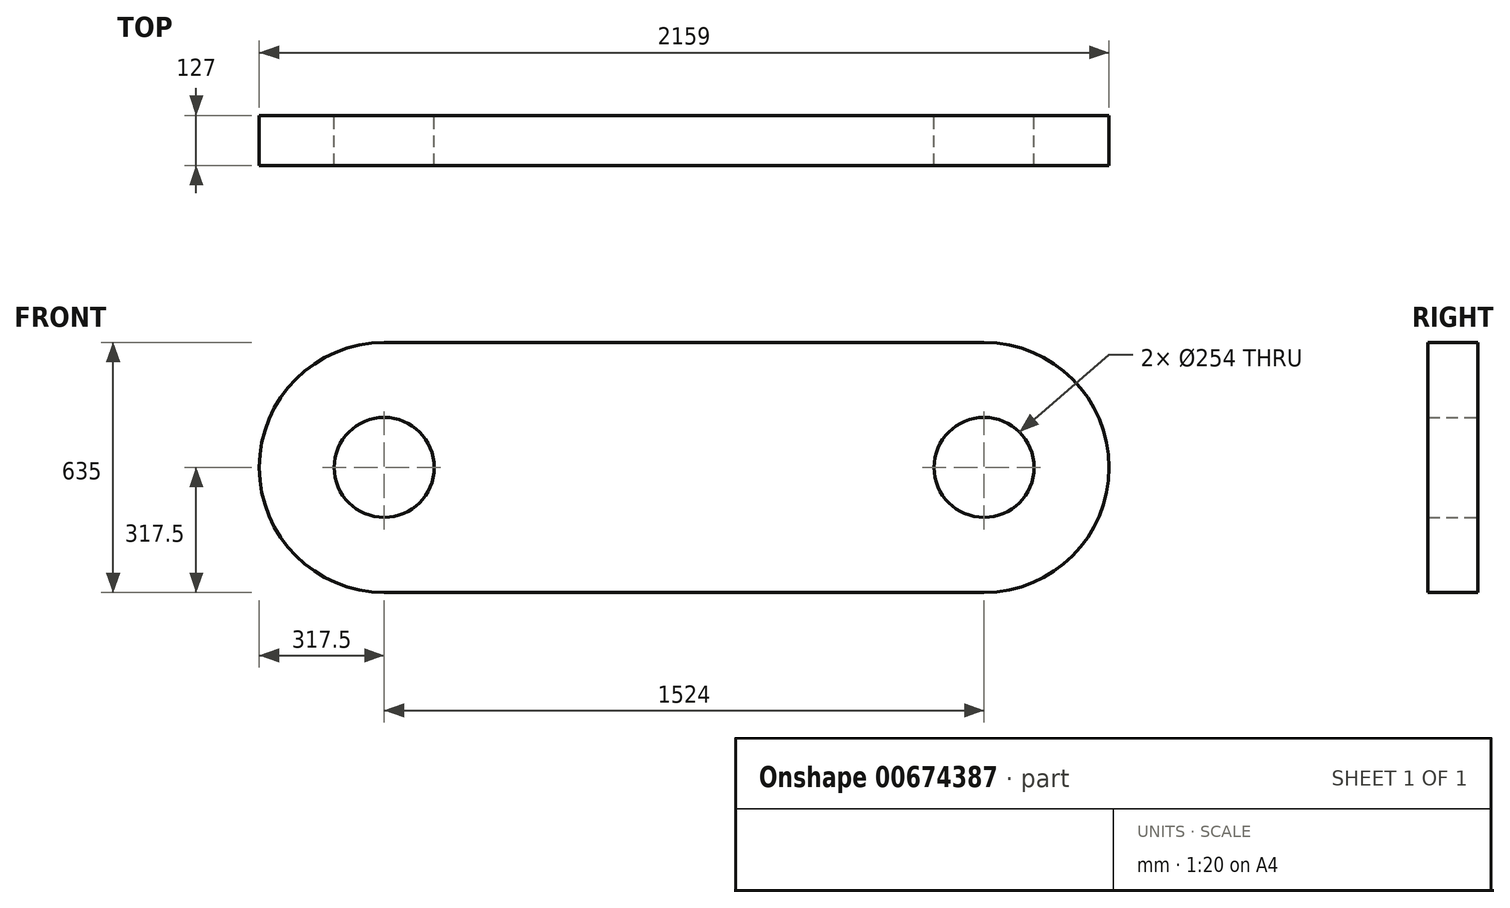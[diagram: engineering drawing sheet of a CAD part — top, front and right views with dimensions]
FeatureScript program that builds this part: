
annotation { "Feature Type Name" : "Feature", "Feature Type Description" : "" }
export const myFeature = defineFeature(function(context is Context, id is Id, definition is map)
    precondition{}
    {
        {
            var Q0;
            Q0=qCreatedBy(makeId("Front.planeOp"),FACE);
            var sketch = newSketch(context, id + "F0", { "sketchPlane" : qUnion([Q0])});
            skLineSegment(sketch, "E0.bottom", {"start": v(762, -317.5) * mm, "end": v(-762, -317.5) * mm});
            skLineSegment(sketch, "E0.top", {"start": v(762, 317.5) * mm, "end": v(-762, 317.5) * mm});
            skPoint(sketch, "E0.middle", {"position": v(0, 0) * mm});
            skArc(sketch, "E1", {"start": v(-762, 317.5) * mm, "mid": v(-1079.5, 0) * mm, "end": v(-762, -317.5) * mm});
            skArc(sketch, "E2", {"start": v(762, -317.5) * mm, "mid": v(1079.5, 0) * mm, "end": v(762, 317.5) * mm});
            skCircle(sketch, "E3", {"center": v(-762, 0) * mm, "radius": 127 * mm});
            skCircle(sketch, "E4", {"center": v(762, 0) * mm, "radius": 127 * mm});
            skSolve(sketch);
        }
        {
            var Q0;
            Q0 = qSketchRegion(id + "F0", true);
            extrude(context, id + "F1", {"entities" : qUnion([Q0]), "endBound" : BoundingType.SYMMETRIC, "depth" : 127 * mm, "offsetDistance" : 25.4 * mm});
        }
    });
